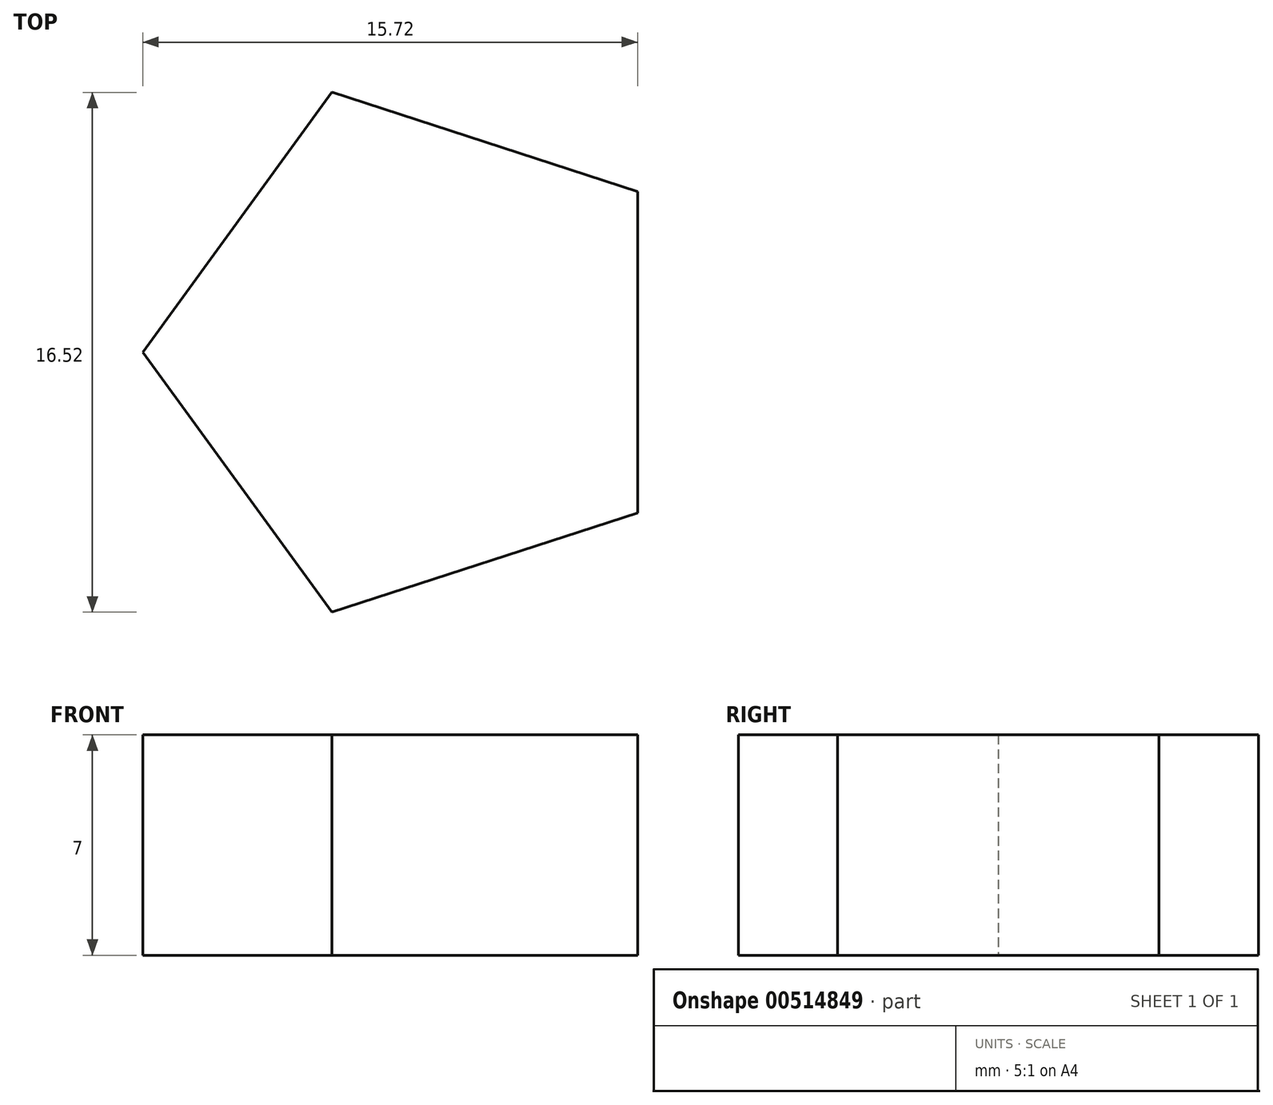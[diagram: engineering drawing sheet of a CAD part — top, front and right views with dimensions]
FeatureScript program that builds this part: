
annotation { "Feature Type Name" : "Feature", "Feature Type Description" : "" }
export const myFeature = defineFeature(function(context is Context, id is Id, definition is map)
    precondition{}
    {
        {
            var Q0;
            Q0=qCreatedBy(makeId("Top.planeOp"),FACE);
            var sketch = newSketch(context, id + "F0", { "sketchPlane" : qUnion([Q0])});
            skCircle(sketch, "E0", {"center": v(0, 0) * mm, "radius": 8.76 * mm});
            skSolve(sketch);
        }
        {
            var Q0;
            Q0=makeQuery(id+"F0.imprint","IMPRINT",FACE,{"disambiguationData":[TD([[makeQuery(id+"F0.imprint","IMPRINT",EDGE,{"derivedFrom":sQuery(id+"F0.wireOp",EDGE,"E0")}),1.0]])]});
            var sketch = newSketch(context, id + "F1", { "sketchPlane" : qUnion([Q0])});
            skCircle(sketch, "E1.cCircle", {"center": v(0, 0) * mm, "radius": 8.69 * mm, "construction": true});
            skLineSegment(sketch, "E1.0", {"start": v(-8.69, 0) * mm, "end": v(-2.68, 8.26) * mm});
            skLineSegment(sketch, "E1.1", {"start": v(-2.68, 8.26) * mm, "end": v(7.03, 5.1) * mm});
            skLineSegment(sketch, "E1.2", {"start": v(7.03, 5.1) * mm, "end": v(7.03, -5.1) * mm});
            skLineSegment(sketch, "E1.3", {"start": v(7.03, -5.1) * mm, "end": v(-2.68, -8.26) * mm});
            skLineSegment(sketch, "E1.4", {"start": v(-2.68, -8.26) * mm, "end": v(-8.69, 0) * mm});
            skSolve(sketch);
        }
        {
            var Q0;
            Q0=makeQuery(id+"F1.imprint","IMPRINT",FACE,{"disambiguationData":[TD([[makeQuery(id+"F1.imprint","IMPRINT",EDGE,{"derivedFrom":sQuery(id+"F1.wireOp",EDGE,"E1.0")}),-1.0]])]});
            extrude(context, id + "F2", {"entities" : qUnion([Q0]), "depth" : 7 * mm, "offsetDistance" : 25 * mm});
        }
    });
